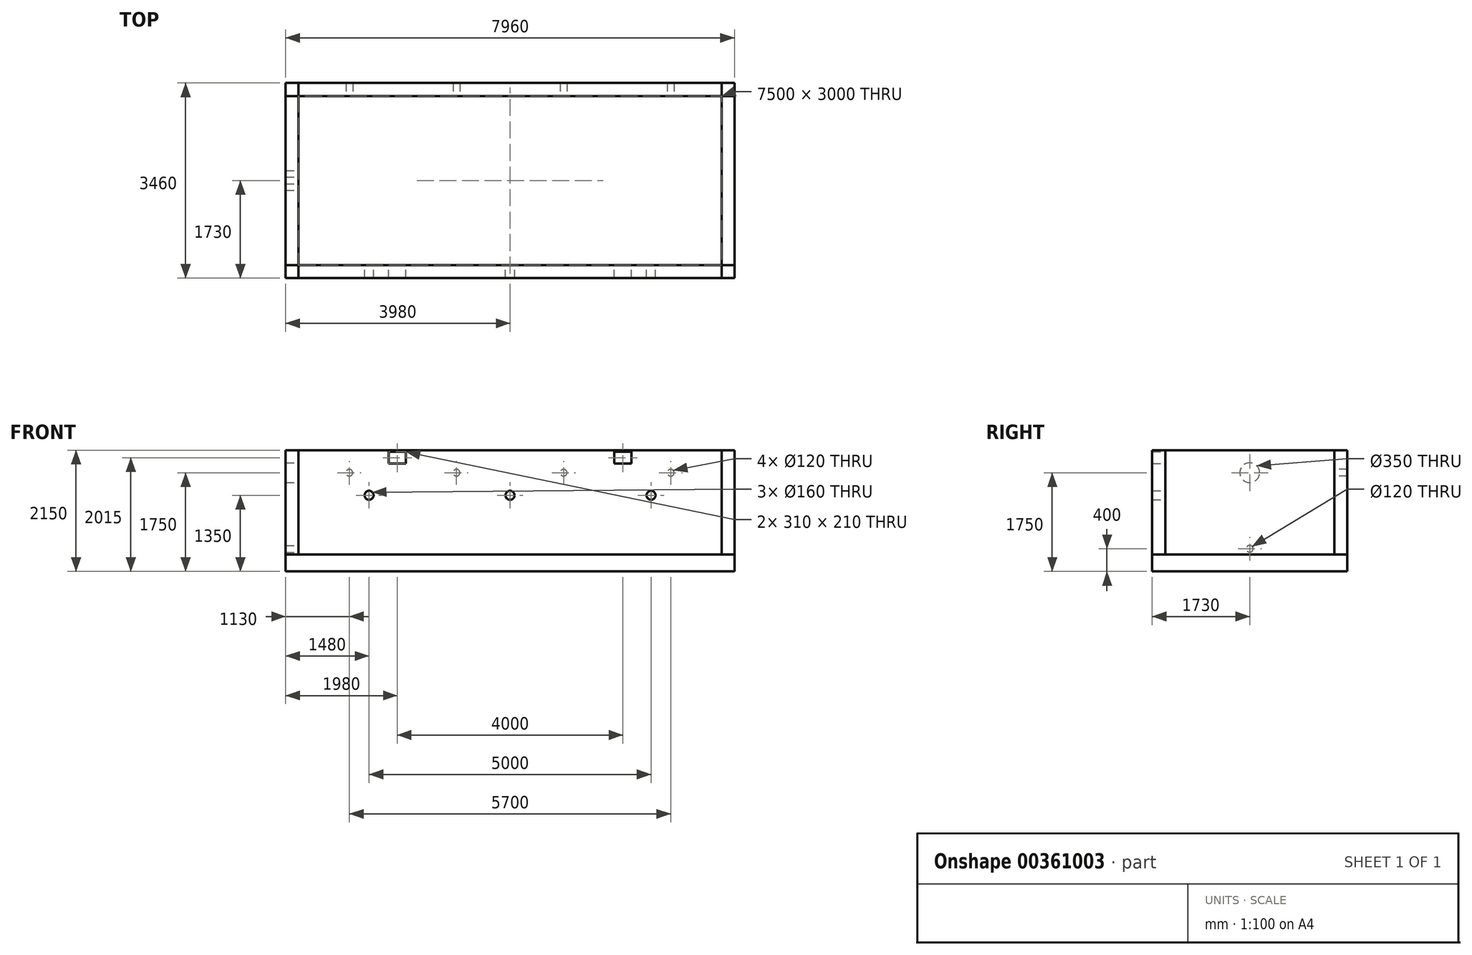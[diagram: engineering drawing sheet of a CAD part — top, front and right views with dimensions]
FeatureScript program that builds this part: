
annotation { "Feature Type Name" : "Feature", "Feature Type Description" : "" }
export const myFeature = defineFeature(function(context is Context, id is Id, definition is map)
    precondition{}
    {
        {
            var Q0;
            Q0=qCreatedBy(makeId("Top.planeOp"),FACE);
            var sketch = newSketch(context, id + "F0", { "sketchPlane" : qUnion([Q0])});
            skLineSegment(sketch, "E0.bottom", {"start": v(-3980, -1730) * mm, "end": v(3980, -1730) * mm});
            skLineSegment(sketch, "E0.top", {"start": v(-3980, 1730) * mm, "end": v(3980, 1730) * mm});
            skLineSegment(sketch, "E0.left", {"start": v(-3980, -1730) * mm, "end": v(-3980, 1730) * mm});
            skLineSegment(sketch, "E0.right", {"start": v(3980, -1730) * mm, "end": v(3980, 1730) * mm});
            skPoint(sketch, "E0.middle", {"position": v(0, 0) * mm});
            skSolve(sketch);
        }
        {
            var Q0;
            Q0 = qSketchRegion(id + "F0", true);
            extrude(context, id + "F1", {"entities" : qUnion([Q0]), "oppositeDirection" : true, "depth" : 300 * mm});
        }
        {
            var Q0;
            Q0=makeQuery(id+"F1.opExtrude","CAP_FACE",FACE,{"disambiguationData":[OSD([sQuery(id+"F0.wireOp",EDGE,"E0.bottom"),sQuery(id+"F0.wireOp",EDGE,"E0.top"),sQuery(id+"F0.wireOp",EDGE,"E0.left"),sQuery(id+"F0.wireOp",EDGE,"E0.right")])],"isStart":true});
            var sketch = newSketch(context, id + "F2", { "sketchPlane" : qUnion([Q0])});
            skLineSegment(sketch, "E1.bottom", {"start": v(-3980, 1730) * mm, "end": v(-3750, 1730) * mm});
            skLineSegment(sketch, "E1.top", {"start": v(-3980, -1730) * mm, "end": v(-3750, -1730) * mm});
            skLineSegment(sketch, "E1.left", {"start": v(-3980, 1730) * mm, "end": v(-3980, -1730) * mm});
            skLineSegment(sketch, "E1.right", {"start": v(-3750, 1730) * mm, "end": v(-3750, -1730) * mm});
            skLineSegment(sketch, "E2.bottom", {"start": v(3980, 1730) * mm, "end": v(3750, 1730) * mm});
            skLineSegment(sketch, "E2.top", {"start": v(3980, -1730) * mm, "end": v(3750, -1730) * mm});
            skLineSegment(sketch, "E2.left", {"start": v(3980, 1730) * mm, "end": v(3980, -1730) * mm});
            skLineSegment(sketch, "E2.right", {"start": v(3750, 1730) * mm, "end": v(3750, -1730) * mm});
            skLineSegment(sketch, "E3.bottom", {"start": v(-3750, 1730) * mm, "end": v(3750, 1730) * mm});
            skLineSegment(sketch, "E3.top", {"start": v(-3750, 1500) * mm, "end": v(3750, 1500) * mm});
            skLineSegment(sketch, "E3.left", {"start": v(-3750, 1730) * mm, "end": v(-3750, 1500) * mm});
            skLineSegment(sketch, "E3.right", {"start": v(3750, 1730) * mm, "end": v(3750, 1500) * mm});
            skLineSegment(sketch, "E4.bottom", {"start": v(-3750, -1730) * mm, "end": v(3750, -1730) * mm});
            skLineSegment(sketch, "E4.top", {"start": v(-3750, -1500) * mm, "end": v(3750, -1500) * mm});
            skLineSegment(sketch, "E4.left", {"start": v(-3750, -1730) * mm, "end": v(-3750, -1500) * mm});
            skLineSegment(sketch, "E4.right", {"start": v(3750, -1730) * mm, "end": v(3750, -1500) * mm});
            skLineSegment(sketch, "E5.bottom", {"start": v(-3750, -1500) * mm, "end": v(-3980, -1500) * mm});
            skLineSegment(sketch, "E5.top", {"start": v(-3750, -1730) * mm, "end": v(-3980, -1730) * mm});
            skLineSegment(sketch, "E5.left", {"start": v(-3750, -1500) * mm, "end": v(-3750, -1730) * mm});
            skLineSegment(sketch, "E5.right", {"start": v(-3980, -1500) * mm, "end": v(-3980, -1730) * mm});
            skLineSegment(sketch, "E6.bottom", {"start": v(-3750, 1500) * mm, "end": v(-3980, 1500) * mm});
            skLineSegment(sketch, "E6.top", {"start": v(-3750, 1730) * mm, "end": v(-3980, 1730) * mm});
            skLineSegment(sketch, "E6.left", {"start": v(-3750, 1500) * mm, "end": v(-3750, 1730) * mm});
            skLineSegment(sketch, "E6.right", {"start": v(-3980, 1500) * mm, "end": v(-3980, 1730) * mm});
            skLineSegment(sketch, "E7.bottom", {"start": v(3750, 1500) * mm, "end": v(3980, 1500) * mm});
            skLineSegment(sketch, "E7.top", {"start": v(3750, 1730) * mm, "end": v(3980, 1730) * mm});
            skLineSegment(sketch, "E7.left", {"start": v(3750, 1500) * mm, "end": v(3750, 1730) * mm});
            skLineSegment(sketch, "E7.right", {"start": v(3980, 1500) * mm, "end": v(3980, 1730) * mm});
            skLineSegment(sketch, "E8.bottom", {"start": v(3750, -1500) * mm, "end": v(3980, -1500) * mm});
            skLineSegment(sketch, "E8.top", {"start": v(3750, -1730) * mm, "end": v(3980, -1730) * mm});
            skLineSegment(sketch, "E8.left", {"start": v(3750, -1500) * mm, "end": v(3750, -1730) * mm});
            skLineSegment(sketch, "E8.right", {"start": v(3980, -1500) * mm, "end": v(3980, -1730) * mm});
            skSolve(sketch);
        }
        {
            var Q0;
            Q0=makeQuery(id+"F2.imprint","IMPRINT",FACE,{"disambiguationData":[TD([[makeQuery(id+"F2.imprint","IMPRINT",EDGE,{"derivedFrom":sQuery(id+"F2.wireOp",EDGE,"E1.left")}),-1.0]])]});
            var Q1;
            Q1=makeQuery(id+"F2.imprint","IMPRINT",FACE,{"disambiguationData":[TD([[makeQuery(id+"F2.imprint","IMPRINT",EDGE,{"derivedFrom":sQuery(id+"F2.wireOp",EDGE,"E2.left")}),1.0]])]});
            var Q2;
            Q2=makeQuery(id+"F2.imprint","IMPRINT",FACE,{"disambiguationData":[TD([[makeQuery(id+"F2.imprint","IMPRINT",EDGE,{"derivedFrom":sQuery(id+"F2.wireOp",EDGE,"E3.bottom")}),-1.0]])]});
            var Q3;
            Q3=makeQuery(id+"F2.imprint","IMPRINT",FACE,{"disambiguationData":[TD([[makeQuery(id+"F2.imprint","IMPRINT",EDGE,{"derivedFrom":sQuery(id+"F2.wireOp",EDGE,"E4.bottom")}),1.0]])]});
            extrude(context, id + "F3", {"entities" : qUnion([Q0, Q1, Q2, Q3]), "depth" : 1850 * mm});
        }
        {
            var Q0;
            Q0=makeQuery(id+"F2.imprint","IMPRINT",FACE,{"disambiguationData":[TD([[makeQuery(id+"F2.imprint","IMPRINT",EDGE,{"derivedFrom":sQuery(id+"F2.wireOp",EDGE,"E5.bottom")}),1.0]])]});
            var Q1;
            Q1=makeQuery(id+"F2.imprint","IMPRINT",FACE,{"disambiguationData":[TD([[makeQuery(id+"F2.imprint","IMPRINT",EDGE,{"derivedFrom":sQuery(id+"F2.wireOp",EDGE,"E6.bottom")}),-1.0]])]});
            var Q2;
            Q2=makeQuery(id+"F2.imprint","IMPRINT",FACE,{"disambiguationData":[TD([[makeQuery(id+"F2.imprint","IMPRINT",EDGE,{"derivedFrom":sQuery(id+"F2.wireOp",EDGE,"E7.bottom")}),1.0]])]});
            var Q3;
            Q3=makeQuery(id+"F2.imprint","IMPRINT",FACE,{"disambiguationData":[TD([[makeQuery(id+"F2.imprint","IMPRINT",EDGE,{"derivedFrom":sQuery(id+"F2.wireOp",EDGE,"E8.bottom")}),-1.0]])]});
            extrude(context, id + "F4", {"entities" : qUnion([Q0, Q1, Q2, Q3]), "depth" : 1850 * mm});
        }
        {
            var Q0;
            Q0=makeQuery(id+"F3.opExtrude","SWEPT_FACE",FACE,{"disambiguationData":[OSD([sQuery(id+"F2.wireOp",EDGE,"E3.top")])]});
            var sketch = newSketch(context, id + "F5", { "sketchPlane" : qUnion([Q0])});
            skLineSegment(sketch, "E9.bottom", {"start": v(-3750, 1850) * mm, "end": v(-2850, 1850) * mm});
            skLineSegment(sketch, "E9.top", {"start": v(-3750, 1450) * mm, "end": v(-2850, 1450) * mm});
            skLineSegment(sketch, "E9.left", {"start": v(-3750, 1850) * mm, "end": v(-3750, 1450) * mm});
            skLineSegment(sketch, "E9.right", {"start": v(-2850, 1850) * mm, "end": v(-2850, 1450) * mm});
            skLineSegment(sketch, "E10.bottom", {"start": v(-2850, 1450) * mm, "end": v(-950, 1450) * mm});
            skLineSegment(sketch, "E10.top", {"start": v(-2850, 1850) * mm, "end": v(-950, 1850) * mm});
            skLineSegment(sketch, "E10.left", {"start": v(-2850, 1450) * mm, "end": v(-2850, 1850) * mm});
            skLineSegment(sketch, "E10.right", {"start": v(-950, 1450) * mm, "end": v(-950, 1850) * mm});
            skLineSegment(sketch, "E11.bottom", {"start": v(-950, 1450) * mm, "end": v(950, 1450) * mm});
            skLineSegment(sketch, "E11.top", {"start": v(-950, 1850) * mm, "end": v(950, 1850) * mm});
            skLineSegment(sketch, "E11.right", {"start": v(950, 1450) * mm, "end": v(950, 1850) * mm});
            skLineSegment(sketch, "E12.bottom", {"start": v(950, 1450) * mm, "end": v(2850, 1450) * mm});
            skLineSegment(sketch, "E12.top", {"start": v(950, 1850) * mm, "end": v(2850, 1850) * mm});
            skLineSegment(sketch, "E12.right", {"start": v(2850, 1450) * mm, "end": v(2850, 1850) * mm});
            skLineSegment(sketch, "E13.bottom", {"start": v(2850, 1450) * mm, "end": v(3750, 1450) * mm});
            skLineSegment(sketch, "E13.top", {"start": v(2850, 1850) * mm, "end": v(3750, 1850) * mm});
            skLineSegment(sketch, "E13.right", {"start": v(3750, 1450) * mm, "end": v(3750, 1850) * mm});
            skCircle(sketch, "E14", {"center": v(-2850, 1450) * mm, "radius": 60 * mm});
            skCircle(sketch, "E15", {"center": v(-950, 1450) * mm, "radius": 60 * mm});
            skCircle(sketch, "E16", {"center": v(950, 1450) * mm, "radius": 60 * mm});
            skCircle(sketch, "E17", {"center": v(2850, 1450) * mm, "radius": 60 * mm});
            skSolve(sketch);
        }
        {
            var Q0;
            {var subQ1=sQuery(id+"F5.wireOp",EDGE,"E9.top");var subQ3=sQuery(id+"F5.wireOp",EDGE,"E14");var subQ4=makeQuery(id+"F5.imprint","INTERSECT",VERTEX,{"derivedFrom":[subQ1,subQ3]});Q0=makeQuery(id+"F5.imprint","IMPRINT",FACE,{"disambiguationData":[TD([[makeQuery(id+"F5.imprint","IMPRINT",EDGE,{"disambiguationData":[TD([[subQ4,-1.0]])],"derivedFrom":subQ3}),1.0]])]});}
            var Q1;
            {var subQ1=sQuery(id+"F5.wireOp",EDGE,"E9.top");var subQ3=sQuery(id+"F5.wireOp",EDGE,"E14");var subQ4=makeQuery(id+"F5.imprint","INTERSECT",VERTEX,{"derivedFrom":[subQ1,subQ3]});Q1=makeQuery(id+"F5.imprint","IMPRINT",FACE,{"disambiguationData":[TD([[makeQuery(id+"F5.imprint","IMPRINT",EDGE,{"disambiguationData":[TD([[subQ4,1.0]])],"derivedFrom":subQ3}),1.0]])]});}
            var Q2;
            {var subQ1=sQuery(id+"F5.wireOp",EDGE,"E10.bottom");var subQ3=sQuery(id+"F5.wireOp",EDGE,"E14");var subQ4=makeQuery(id+"F5.imprint","INTERSECT",VERTEX,{"derivedFrom":[subQ1,subQ3]});Q2=makeQuery(id+"F5.imprint","IMPRINT",FACE,{"disambiguationData":[TD([[makeQuery(id+"F5.imprint","IMPRINT",EDGE,{"disambiguationData":[TD([[subQ4,-1.0]])],"derivedFrom":subQ3}),1.0]])]});}
            var Q3;
            {var subQ1=sQuery(id+"F5.wireOp",EDGE,"E10.bottom");var subQ3=sQuery(id+"F5.wireOp",EDGE,"E15");var subQ4=makeQuery(id+"F5.imprint","INTERSECT",VERTEX,{"derivedFrom":[subQ1,subQ3]});Q3=makeQuery(id+"F5.imprint","IMPRINT",FACE,{"disambiguationData":[TD([[makeQuery(id+"F5.imprint","IMPRINT",EDGE,{"disambiguationData":[TD([[subQ4,-1.0]])],"derivedFrom":subQ3}),1.0]])]});}
            var Q4;
            {var subQ1=sQuery(id+"F5.wireOp",EDGE,"E10.bottom");var subQ3=sQuery(id+"F5.wireOp",EDGE,"E15");var subQ4=makeQuery(id+"F5.imprint","INTERSECT",VERTEX,{"derivedFrom":[subQ1,subQ3]});Q4=makeQuery(id+"F5.imprint","IMPRINT",FACE,{"disambiguationData":[TD([[makeQuery(id+"F5.imprint","IMPRINT",EDGE,{"disambiguationData":[TD([[subQ4,1.0]])],"derivedFrom":subQ3}),1.0]])]});}
            var Q5;
            {var subQ1=sQuery(id+"F5.wireOp",EDGE,"E11.bottom");var subQ3=sQuery(id+"F5.wireOp",EDGE,"E15");var subQ4=makeQuery(id+"F5.imprint","INTERSECT",VERTEX,{"derivedFrom":[subQ1,subQ3]});Q5=makeQuery(id+"F5.imprint","IMPRINT",FACE,{"disambiguationData":[TD([[makeQuery(id+"F5.imprint","IMPRINT",EDGE,{"disambiguationData":[TD([[subQ4,-1.0]])],"derivedFrom":subQ3}),1.0]])]});}
            var Q6;
            {var subQ1=sQuery(id+"F5.wireOp",EDGE,"E11.bottom");var subQ3=sQuery(id+"F5.wireOp",EDGE,"E16");var subQ4=makeQuery(id+"F5.imprint","INTERSECT",VERTEX,{"derivedFrom":[subQ1,subQ3]});Q6=makeQuery(id+"F5.imprint","IMPRINT",FACE,{"disambiguationData":[TD([[makeQuery(id+"F5.imprint","IMPRINT",EDGE,{"disambiguationData":[TD([[subQ4,-1.0]])],"derivedFrom":subQ3}),1.0]])]});}
            var Q7;
            {var subQ1=sQuery(id+"F5.wireOp",EDGE,"E11.bottom");var subQ3=sQuery(id+"F5.wireOp",EDGE,"E16");var subQ4=makeQuery(id+"F5.imprint","INTERSECT",VERTEX,{"derivedFrom":[subQ1,subQ3]});Q7=makeQuery(id+"F5.imprint","IMPRINT",FACE,{"disambiguationData":[TD([[makeQuery(id+"F5.imprint","IMPRINT",EDGE,{"disambiguationData":[TD([[subQ4,1.0]])],"derivedFrom":subQ3}),1.0]])]});}
            var Q8;
            {var subQ1=sQuery(id+"F5.wireOp",EDGE,"E12.bottom");var subQ3=sQuery(id+"F5.wireOp",EDGE,"E16");var subQ4=makeQuery(id+"F5.imprint","INTERSECT",VERTEX,{"derivedFrom":[subQ1,subQ3]});Q8=makeQuery(id+"F5.imprint","IMPRINT",FACE,{"disambiguationData":[TD([[makeQuery(id+"F5.imprint","IMPRINT",EDGE,{"disambiguationData":[TD([[subQ4,-1.0]])],"derivedFrom":subQ3}),1.0]])]});}
            var Q9;
            {var subQ1=sQuery(id+"F5.wireOp",EDGE,"E12.bottom");var subQ3=sQuery(id+"F5.wireOp",EDGE,"E17");var subQ4=makeQuery(id+"F5.imprint","INTERSECT",VERTEX,{"derivedFrom":[subQ1,subQ3]});Q9=makeQuery(id+"F5.imprint","IMPRINT",FACE,{"disambiguationData":[TD([[makeQuery(id+"F5.imprint","IMPRINT",EDGE,{"disambiguationData":[TD([[subQ4,-1.0]])],"derivedFrom":subQ3}),1.0]])]});}
            var Q10;
            {var subQ1=sQuery(id+"F5.wireOp",EDGE,"E12.bottom");var subQ3=sQuery(id+"F5.wireOp",EDGE,"E17");var subQ4=makeQuery(id+"F5.imprint","INTERSECT",VERTEX,{"derivedFrom":[subQ1,subQ3]});Q10=makeQuery(id+"F5.imprint","IMPRINT",FACE,{"disambiguationData":[TD([[makeQuery(id+"F5.imprint","IMPRINT",EDGE,{"disambiguationData":[TD([[subQ4,1.0]])],"derivedFrom":subQ3}),1.0]])]});}
            var Q11;
            {var subQ1=sQuery(id+"F5.wireOp",EDGE,"E13.bottom");var subQ3=sQuery(id+"F5.wireOp",EDGE,"E17");var subQ4=makeQuery(id+"F5.imprint","INTERSECT",VERTEX,{"derivedFrom":[subQ1,subQ3]});Q11=makeQuery(id+"F5.imprint","IMPRINT",FACE,{"disambiguationData":[TD([[makeQuery(id+"F5.imprint","IMPRINT",EDGE,{"disambiguationData":[TD([[subQ4,-1.0]])],"derivedFrom":subQ3}),1.0]])]});}
            extrude(context, id + "F6", {"entities" : qUnion([Q0, Q1, Q2, Q3, Q4, Q5, Q6, Q7, Q8, Q9, Q10, Q11]), "operationType" : NewBodyOperationType.REMOVE, "oppositeDirection" : true, "depth" : 230 * mm});
        }
        {
            var Q0;
            Q0=makeQuery(id+"F3.opExtrude","SWEPT_FACE",FACE,{"disambiguationData":[OSD([sQuery(id+"F2.wireOp",EDGE,"E4.top")])]});
            var sketch = newSketch(context, id + "F7", { "sketchPlane" : qUnion([Q0])});
            skLineSegment(sketch, "E18.bottom", {"start": v(-3750, 1850) * mm, "end": v(-2500, 1850) * mm});
            skLineSegment(sketch, "E18.top", {"start": v(-3750, 1050) * mm, "end": v(-2500, 1050) * mm});
            skLineSegment(sketch, "E18.left", {"start": v(-3750, 1850) * mm, "end": v(-3750, 1050) * mm});
            skLineSegment(sketch, "E18.right", {"start": v(-2500, 1850) * mm, "end": v(-2500, 1050) * mm});
            skLineSegment(sketch, "E19.bottom", {"start": v(-2500, 1050) * mm, "end": v(0, 1050) * mm});
            skLineSegment(sketch, "E19.top", {"start": v(-2500, 1850) * mm, "end": v(0, 1850) * mm});
            skLineSegment(sketch, "E19.left", {"start": v(-2500, 1050) * mm, "end": v(-2500, 1850) * mm});
            skLineSegment(sketch, "E19.right", {"start": v(0, 1050) * mm, "end": v(0, 1850) * mm});
            skLineSegment(sketch, "E20.bottom", {"start": v(0, 1050) * mm, "end": v(2500, 1050) * mm});
            skLineSegment(sketch, "E20.top", {"start": v(0, 1850) * mm, "end": v(2500, 1850) * mm});
            skLineSegment(sketch, "E20.right", {"start": v(2500, 1050) * mm, "end": v(2500, 1850) * mm});
            skLineSegment(sketch, "E21.bottom", {"start": v(2500, 1050) * mm, "end": v(3750, 1050) * mm});
            skLineSegment(sketch, "E21.top", {"start": v(2500, 1850) * mm, "end": v(3750, 1850) * mm});
            skLineSegment(sketch, "E21.right", {"start": v(3750, 1050) * mm, "end": v(3750, 1850) * mm});
            skCircle(sketch, "E22", {"center": v(-2500, 1050) * mm, "radius": 80 * mm});
            skCircle(sketch, "E23", {"center": v(0, 1050) * mm, "radius": 80 * mm});
            skCircle(sketch, "E24", {"center": v(2500, 1050) * mm, "radius": 80 * mm});
            skLineSegment(sketch, "E25.bottom", {"start": v(-3750, 1850) * mm, "end": v(-2000, 1850) * mm});
            skLineSegment(sketch, "E25.top", {"start": v(-3750, 1715) * mm, "end": v(-2000, 1715) * mm});
            skLineSegment(sketch, "E25.left", {"start": v(-3750, 1850) * mm, "end": v(-3750, 1715) * mm});
            skLineSegment(sketch, "E25.right", {"start": v(-2000, 1850) * mm, "end": v(-2000, 1715) * mm});
            skLineSegment(sketch, "E26.bottom", {"start": v(-1845, 1610) * mm, "end": v(-2155, 1610) * mm});
            skLineSegment(sketch, "E26.top", {"start": v(-1845, 1820) * mm, "end": v(-2155, 1820) * mm});
            skLineSegment(sketch, "E26.left", {"start": v(-1845, 1610) * mm, "end": v(-1845, 1820) * mm});
            skLineSegment(sketch, "E26.right", {"start": v(-2155, 1610) * mm, "end": v(-2155, 1820) * mm});
            skPoint(sketch, "E26.middle", {"position": v(-2000, 1715) * mm});
            skLineSegment(sketch, "E27.bottom", {"start": v(3750, 1850) * mm, "end": v(2000, 1850) * mm});
            skLineSegment(sketch, "E27.top", {"start": v(3750, 1715) * mm, "end": v(2000, 1715) * mm});
            skLineSegment(sketch, "E27.left", {"start": v(3750, 1850) * mm, "end": v(3750, 1715) * mm});
            skLineSegment(sketch, "E27.right", {"start": v(2000, 1850) * mm, "end": v(2000, 1715) * mm});
            skLineSegment(sketch, "E28.bottom", {"start": v(1845, 1610) * mm, "end": v(2155, 1610) * mm});
            skLineSegment(sketch, "E28.top", {"start": v(1845, 1820) * mm, "end": v(2155, 1820) * mm});
            skLineSegment(sketch, "E28.left", {"start": v(1845, 1610) * mm, "end": v(1845, 1820) * mm});
            skLineSegment(sketch, "E28.right", {"start": v(2155, 1610) * mm, "end": v(2155, 1820) * mm});
            skPoint(sketch, "E28.middle", {"position": v(2000, 1715) * mm});
            skSolve(sketch);
        }
        {
            var Q0;
            {var subQ1=sQuery(id+"F7.wireOp",EDGE,"E18.top");var subQ3=sQuery(id+"F7.wireOp",EDGE,"E22");var subQ4=makeQuery(id+"F7.imprint","INTERSECT",VERTEX,{"derivedFrom":[subQ1,subQ3]});Q0=makeQuery(id+"F7.imprint","IMPRINT",FACE,{"disambiguationData":[TD([[makeQuery(id+"F7.imprint","IMPRINT",EDGE,{"disambiguationData":[TD([[subQ4,1.0]])],"derivedFrom":subQ3}),1.0]])]});}
            var Q1;
            {var subQ1=sQuery(id+"F7.wireOp",EDGE,"E19.bottom");var subQ3=sQuery(id+"F7.wireOp",EDGE,"E22");var subQ4=makeQuery(id+"F7.imprint","INTERSECT",VERTEX,{"derivedFrom":[subQ1,subQ3]});Q1=makeQuery(id+"F7.imprint","IMPRINT",FACE,{"disambiguationData":[TD([[makeQuery(id+"F7.imprint","IMPRINT",EDGE,{"disambiguationData":[TD([[subQ4,-1.0]])],"derivedFrom":subQ3}),1.0]])]});}
            var Q2;
            {var subQ1=sQuery(id+"F7.wireOp",EDGE,"E18.top");var subQ3=sQuery(id+"F7.wireOp",EDGE,"E22");var subQ4=makeQuery(id+"F7.imprint","INTERSECT",VERTEX,{"derivedFrom":[subQ1,subQ3]});Q2=makeQuery(id+"F7.imprint","IMPRINT",FACE,{"disambiguationData":[TD([[makeQuery(id+"F7.imprint","IMPRINT",EDGE,{"disambiguationData":[TD([[subQ4,-1.0]])],"derivedFrom":subQ3}),1.0]])]});}
            var Q3;
            {var subQ1=sQuery(id+"F7.wireOp",EDGE,"E19.bottom");var subQ3=sQuery(id+"F7.wireOp",EDGE,"E23");var subQ4=makeQuery(id+"F7.imprint","INTERSECT",VERTEX,{"derivedFrom":[subQ1,subQ3]});Q3=makeQuery(id+"F7.imprint","IMPRINT",FACE,{"disambiguationData":[TD([[makeQuery(id+"F7.imprint","IMPRINT",EDGE,{"disambiguationData":[TD([[subQ4,1.0]])],"derivedFrom":subQ3}),1.0]])]});}
            var Q4;
            {var subQ1=sQuery(id+"F7.wireOp",EDGE,"E19.bottom");var subQ3=sQuery(id+"F7.wireOp",EDGE,"E23");var subQ4=makeQuery(id+"F7.imprint","INTERSECT",VERTEX,{"derivedFrom":[subQ1,subQ3]});Q4=makeQuery(id+"F7.imprint","IMPRINT",FACE,{"disambiguationData":[TD([[makeQuery(id+"F7.imprint","IMPRINT",EDGE,{"disambiguationData":[TD([[subQ4,-1.0]])],"derivedFrom":subQ3}),1.0]])]});}
            var Q5;
            {var subQ1=sQuery(id+"F7.wireOp",EDGE,"E20.bottom");var subQ3=sQuery(id+"F7.wireOp",EDGE,"E23");var subQ4=makeQuery(id+"F7.imprint","INTERSECT",VERTEX,{"derivedFrom":[subQ1,subQ3]});Q5=makeQuery(id+"F7.imprint","IMPRINT",FACE,{"disambiguationData":[TD([[makeQuery(id+"F7.imprint","IMPRINT",EDGE,{"disambiguationData":[TD([[subQ4,-1.0]])],"derivedFrom":subQ3}),1.0]])]});}
            var Q6;
            {var subQ1=sQuery(id+"F7.wireOp",EDGE,"E20.bottom");var subQ3=sQuery(id+"F7.wireOp",EDGE,"E24");var subQ4=makeQuery(id+"F7.imprint","INTERSECT",VERTEX,{"derivedFrom":[subQ1,subQ3]});Q6=makeQuery(id+"F7.imprint","IMPRINT",FACE,{"disambiguationData":[TD([[makeQuery(id+"F7.imprint","IMPRINT",EDGE,{"disambiguationData":[TD([[subQ4,-1.0]])],"derivedFrom":subQ3}),1.0]])]});}
            var Q7;
            {var subQ1=sQuery(id+"F7.wireOp",EDGE,"E20.bottom");var subQ3=sQuery(id+"F7.wireOp",EDGE,"E24");var subQ4=makeQuery(id+"F7.imprint","INTERSECT",VERTEX,{"derivedFrom":[subQ1,subQ3]});Q7=makeQuery(id+"F7.imprint","IMPRINT",FACE,{"disambiguationData":[TD([[makeQuery(id+"F7.imprint","IMPRINT",EDGE,{"disambiguationData":[TD([[subQ4,1.0]])],"derivedFrom":subQ3}),1.0]])]});}
            var Q8;
            {var subQ1=sQuery(id+"F7.wireOp",EDGE,"E21.bottom");var subQ3=sQuery(id+"F7.wireOp",EDGE,"E24");var subQ4=makeQuery(id+"F7.imprint","INTERSECT",VERTEX,{"derivedFrom":[subQ1,subQ3]});Q8=makeQuery(id+"F7.imprint","IMPRINT",FACE,{"disambiguationData":[TD([[makeQuery(id+"F7.imprint","IMPRINT",EDGE,{"disambiguationData":[TD([[subQ4,-1.0]])],"derivedFrom":subQ3}),1.0]])]});}
            extrude(context, id + "F8", {"entities" : qUnion([Q0, Q1, Q2, Q3, Q4, Q5, Q6, Q7, Q8]), "operationType" : NewBodyOperationType.REMOVE, "oppositeDirection" : true, "depth" : 230 * mm});
        }
        {
            var Q0;
            {var subQ0=sQuery(id+"F7.wireOp",EDGE,"E28.bottom");Q0=makeQuery(id+"F7.imprint","IMPRINT",FACE,{"disambiguationData":[TD([[makeQuery(id+"F7.imprint","IMPRINT",EDGE,{"derivedFrom":subQ0}),1.0]])]});}
            var Q1;
            {var subQ0=sQuery(id+"F7.wireOp",EDGE,"E27.right");var subQ1=sQuery(id+"F7.wireOp",EDGE,"E27.top");var subQ2=makeQuery(id+"F7.imprint","INTERSECT",VERTEX,{"derivedFrom":[subQ1,subQ0]});Q1=makeQuery(id+"F7.imprint","IMPRINT",FACE,{"disambiguationData":[TD([[makeQuery(id+"F7.imprint","IMPRINT",EDGE,{"disambiguationData":[TD([[subQ2,1.0]])],"derivedFrom":subQ1}),-1.0]])]});}
            var Q2;
            {var subQ0=sQuery(id+"F7.wireOp",EDGE,"E26.bottom");Q2=makeQuery(id+"F7.imprint","IMPRINT",FACE,{"disambiguationData":[TD([[makeQuery(id+"F7.imprint","IMPRINT",EDGE,{"derivedFrom":subQ0}),-1.0]])]});}
            var Q3;
            {var subQ0=sQuery(id+"F7.wireOp",EDGE,"E25.right");var subQ1=sQuery(id+"F7.wireOp",EDGE,"E25.top");var subQ2=makeQuery(id+"F7.imprint","INTERSECT",VERTEX,{"derivedFrom":[subQ1,subQ0]});Q3=makeQuery(id+"F7.imprint","IMPRINT",FACE,{"disambiguationData":[TD([[makeQuery(id+"F7.imprint","IMPRINT",EDGE,{"disambiguationData":[TD([[subQ2,1.0]])],"derivedFrom":subQ1}),1.0]])]});}
            extrude(context, id + "F9", {"entities" : qUnion([Q0, Q1, Q2, Q3]), "operationType" : NewBodyOperationType.REMOVE, "oppositeDirection" : true, "depth" : 230 * mm});
        }
        {
            var Q0;
            Q0=makeQuery(id+"F3.opExtrude","SWEPT_FACE",FACE,{"disambiguationData":[OSD([sQuery(id+"F2.wireOp",EDGE,"E1.right")])]});
            var sketch = newSketch(context, id + "F10", { "sketchPlane" : qUnion([Q0])});
            skPoint(sketch, "E29.oppositeSnap0", {"position": v(0, 1850) * mm});
            skLineSegment(sketch, "E29.bottom", {"start": v(1500, 1850) * mm, "end": v(0, 1850) * mm});
            skLineSegment(sketch, "E29.top", {"start": v(1500, 1450) * mm, "end": v(0, 1450) * mm});
            skLineSegment(sketch, "E29.left", {"start": v(1500, 1850) * mm, "end": v(1500, 1450) * mm});
            skLineSegment(sketch, "E29.right", {"start": v(0, 1850) * mm, "end": v(0, 1450) * mm});
            skCircle(sketch, "E30", {"center": v(0, 1450) * mm, "radius": 175 * mm});
            skPoint(sketch, "E31.oppositeSnap0", {"position": v(0, 0) * mm});
            skLineSegment(sketch, "E31.bottom", {"start": v(1500, 0) * mm, "end": v(0, 0) * mm});
            skLineSegment(sketch, "E31.top", {"start": v(1500, 100) * mm, "end": v(0, 100) * mm});
            skLineSegment(sketch, "E31.left", {"start": v(1500, 0) * mm, "end": v(1500, 100) * mm});
            skLineSegment(sketch, "E31.right", {"start": v(0, 0) * mm, "end": v(0, 100) * mm});
            skCircle(sketch, "E32", {"center": v(0, 100) * mm, "radius": 60 * mm});
            skSolve(sketch);
        }
        {
            var Q0;
            {var subQ0=sQuery(id+"F10.wireOp",EDGE,"E31.right");var subQ1=sQuery(id+"F10.wireOp",EDGE,"E31.top");var subQ2=makeQuery(id+"F10.imprint","INTERSECT",VERTEX,{"derivedFrom":[subQ1,subQ0]});Q0=makeQuery(id+"F10.imprint","IMPRINT",FACE,{"disambiguationData":[TD([[makeQuery(id+"F10.imprint","IMPRINT",EDGE,{"disambiguationData":[TD([[subQ2,1.0]])],"derivedFrom":subQ1}),-1.0]])]});}
            var Q1;
            {var subQ0=sQuery(id+"F10.wireOp",EDGE,"E31.right");var subQ1=sQuery(id+"F10.wireOp",EDGE,"E31.top");var subQ2=makeQuery(id+"F10.imprint","INTERSECT",VERTEX,{"derivedFrom":[subQ1,subQ0]});Q1=makeQuery(id+"F10.imprint","IMPRINT",FACE,{"disambiguationData":[TD([[makeQuery(id+"F10.imprint","IMPRINT",EDGE,{"disambiguationData":[TD([[subQ2,1.0]])],"derivedFrom":subQ1}),1.0]])]});}
            var Q2;
            {var subQ0=sQuery(id+"F10.wireOp",EDGE,"E29.right");var subQ1=sQuery(id+"F10.wireOp",EDGE,"E29.top");var subQ2=makeQuery(id+"F10.imprint","INTERSECT",VERTEX,{"derivedFrom":[subQ1,subQ0]});Q2=makeQuery(id+"F10.imprint","IMPRINT",FACE,{"disambiguationData":[TD([[makeQuery(id+"F10.imprint","IMPRINT",EDGE,{"disambiguationData":[TD([[subQ2,1.0]])],"derivedFrom":subQ1}),1.0]])]});}
            var Q3;
            {var subQ0=sQuery(id+"F10.wireOp",EDGE,"E29.right");var subQ1=sQuery(id+"F10.wireOp",EDGE,"E29.top");var subQ2=makeQuery(id+"F10.imprint","INTERSECT",VERTEX,{"derivedFrom":[subQ1,subQ0]});Q3=makeQuery(id+"F10.imprint","IMPRINT",FACE,{"disambiguationData":[TD([[makeQuery(id+"F10.imprint","IMPRINT",EDGE,{"disambiguationData":[TD([[subQ2,1.0]])],"derivedFrom":subQ1}),-1.0]])]});}
            extrude(context, id + "F11", {"entities" : qUnion([Q0, Q1, Q2, Q3]), "operationType" : NewBodyOperationType.REMOVE, "oppositeDirection" : true, "depth" : 230 * mm});
        }
    });
